# Revit family: Masonry-Fireplace
name_source: partatom
category: Mechanical Equipment
units: mm (PartAtom-declared; Revit-internal decimal feet)

## family parameters
Always vertical = Yes
Classification Number = 23.40.20.34.14
Cut with Voids When Loaded = No
Maintain Annotation Orientation = No
Part Type = Normal
Room Calculation Point = No
Round Connector Dimension = Use Diameter
Shared = No
Work Plane-Based = No

## types (1)
- Masonry-Fireplace
    Assembly Code = D3020
    Chimney Structure Material = Masonry - Concrete Masonry Units
    Construction Details = http://www.arcat.com
    Default Elevation = 0' - 0"
    Description = Masonry Fireplace
    Expected Lifespan (Years) = 75
    Firebox Back Height = 0' - 10 21/32"
    Firebox Back Width = 1' - 2"
    Firebox Depth = 2' - 0"
    Firebox Height = 2' - 8"
    Firebox Material = Masonry - Firebrick
    Firebox Width = 3' - 6"
    Firebrick Width = 0' - 3"
    Flue D = 0' - 9 3/32"
    Flue W = 0' - 9 19/32"
    FlueRad = 0' - 8"
    Foundation to TO Smoke Chamber = 4' - 4"
    Green Building - LEED = http://www.arcat.com
    Hearth Extension = 1' - 4"
    Hearth Height from Finished Floor = 0' - 6"
    Keynote = 04880
    Maintenance Schedule (Months) = 0
    Manufacturer = Generic
    Manufacturer Fax = (203) 939-2444
    Manufacturer Website = http://www.arcat.com
    Model = Generic
    Outer Wall Thickness = 0' - 4"
    Product Data = http://www.arcat.com
    Product Properties = http://www.arcat.com
    Projection into Living Space = 0' - 4"
    Slab Material = ARCAT - Concrete - Cast-in-Place Concrete
    Slab Thickness = 0' - 3"
    Smoke Shelf Height = 1' - 2"
    Specification = http://www.arcat.com
    URL = http://www.arcat.com
    Warranty Duration (Years) = 0

## geometry (parser evidence)
native form markers: Sweep x4
no freeform markers — native parametric forms only
